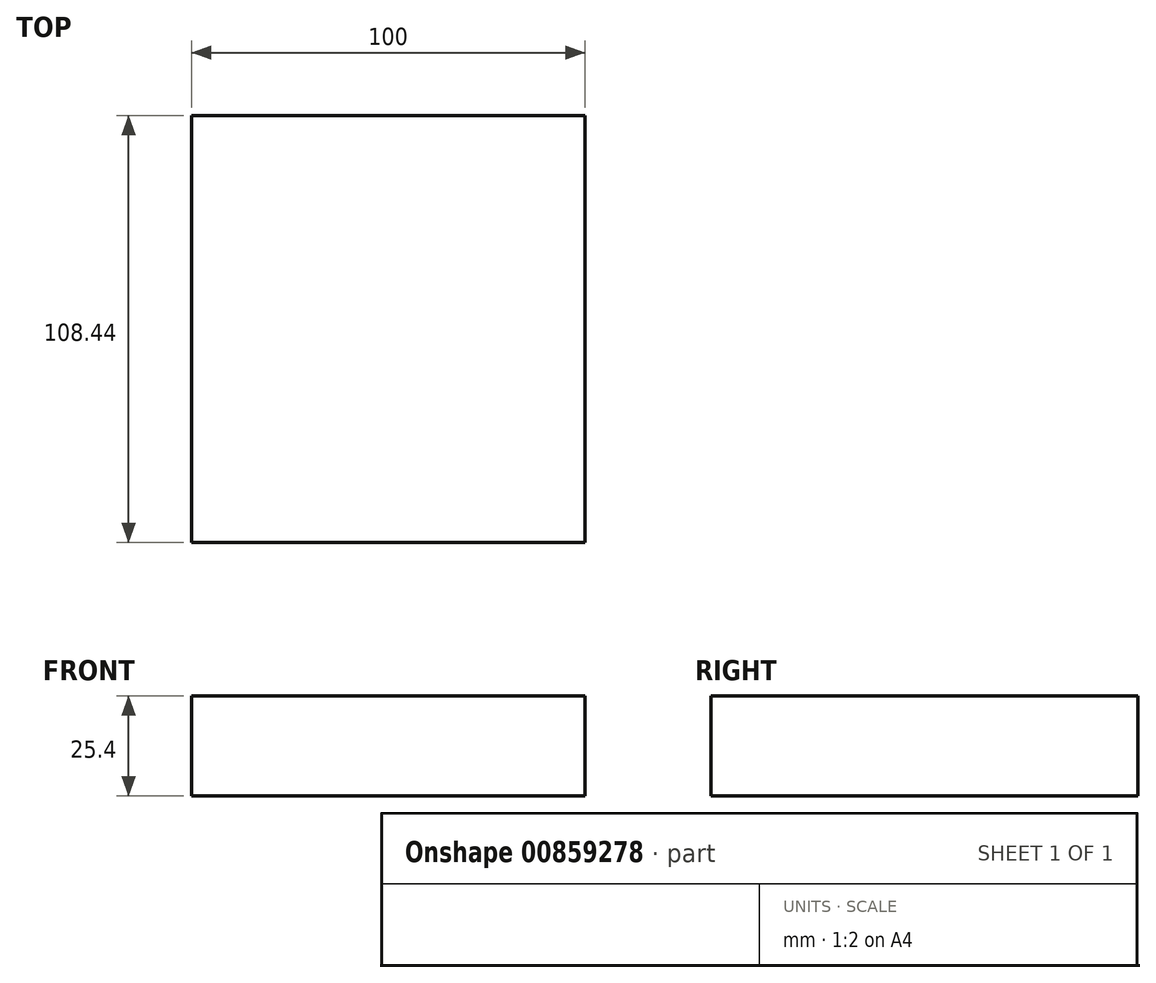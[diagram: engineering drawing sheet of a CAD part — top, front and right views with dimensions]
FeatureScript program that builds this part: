
annotation { "Feature Type Name" : "Feature", "Feature Type Description" : "" }
export const myFeature = defineFeature(function(context is Context, id is Id, definition is map)
    precondition{}
    {
        {
            var Q0;
            Q0=qCreatedBy(makeId("Top.planeOp"),FACE);
            var sketch = newSketch(context, id + "F0", { "sketchPlane" : qUnion([Q0])});
            skLineSegment(sketch, "E0.bottom", {"start": v(50, -54.22) * mm, "end": v(-50, -54.22) * mm});
            skLineSegment(sketch, "E0.top", {"start": v(50, 54.22) * mm, "end": v(-50, 54.22) * mm});
            skLineSegment(sketch, "E0.left", {"start": v(50, -54.22) * mm, "end": v(50, 54.22) * mm});
            skLineSegment(sketch, "E0.right", {"start": v(-50, -54.22) * mm, "end": v(-50, 54.22) * mm});
            skPoint(sketch, "E0.middle", {"position": v(0, 0) * mm});
            skSolve(sketch);
        }
        {
            var Q0;
            Q0=makeQuery(id+"F0.imprint","IMPRINT",FACE,{"disambiguationData":[TD([[makeQuery(id+"F0.imprint","IMPRINT",EDGE,{"derivedFrom":sQuery(id+"F0.wireOp",EDGE,"E0.bottom")}),-1.0]])]});
            extrude(context, id + "F1", {"entities" : qUnion([Q0]), "depth" : 25.4 * mm, "offsetDistance" : 25.4 * mm});
        }
    });
